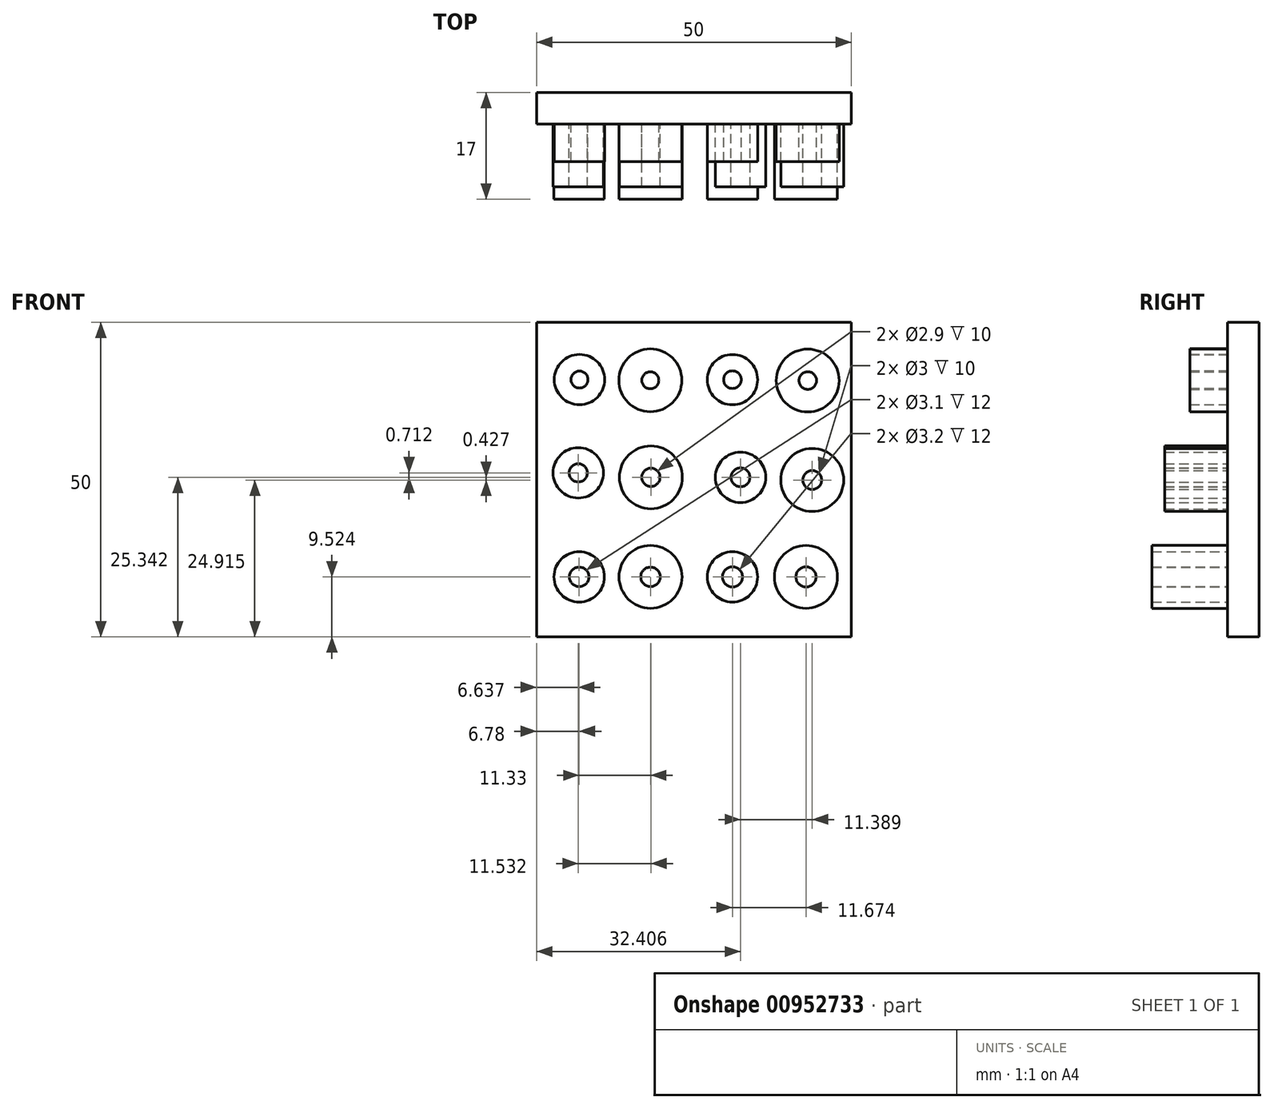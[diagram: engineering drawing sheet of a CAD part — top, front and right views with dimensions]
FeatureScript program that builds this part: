
annotation { "Feature Type Name" : "Feature", "Feature Type Description" : "" }
export const myFeature = defineFeature(function(context is Context, id is Id, definition is map)
    precondition{}
    {
        {
            var Q0;
            Q0=qCreatedBy(makeId("Front.planeOp"),FACE);
            var sketch = newSketch(context, id + "F0", { "sketchPlane" : qUnion([Q0])});
            skLineSegment(sketch, "E0.bottom", {"start": v(-25, 25) * mm, "end": v(25, 25) * mm});
            skLineSegment(sketch, "E0.top", {"start": v(-25, -25) * mm, "end": v(25, -25) * mm});
            skLineSegment(sketch, "E0.left", {"start": v(-25, 25) * mm, "end": v(-25, -25) * mm});
            skLineSegment(sketch, "E0.right", {"start": v(25, 25) * mm, "end": v(25, -25) * mm});
            skSolve(sketch);
        }
        {
            var Q0;
            Q0=qCreatedBy(makeId("Front.planeOp"),FACE);
            var sketch = newSketch(context, id + "F1", { "sketchPlane" : qUnion([Q0])});
            skPoint(sketch, "E1.middle", {"position": v(0.42, -1.18) * mm});
            skCircle(sketch, "E2", {"center": v(-18.17, 15.87) * mm, "radius": 1.35 * mm});
            skCircle(sketch, "E3", {"center": v(-18.17, 15.87) * mm, "radius": 4 * mm});
            skCircle(sketch, "E4", {"center": v(-6.92, 15.76) * mm, "radius": 5 * mm});
            skCircle(sketch, "E5", {"center": v(-6.92, 15.76) * mm, "radius": 1.35 * mm});
            skCircle(sketch, "E6", {"center": v(6.12, 15.86) * mm, "radius": 4 * mm});
            skCircle(sketch, "E7", {"center": v(6.12, 15.86) * mm, "radius": 1.4 * mm});
            skCircle(sketch, "E8", {"center": v(18.08, 15.72) * mm, "radius": 5 * mm});
            skCircle(sketch, "E9", {"center": v(18.08, 15.72) * mm, "radius": 1.4 * mm});
            skCircle(sketch, "E10", {"center": v(-18.36, 1.05) * mm, "radius": 4 * mm});
            skCircle(sketch, "E11", {"center": v(-18.36, 1.05) * mm, "radius": 1.45 * mm});
            skCircle(sketch, "E12", {"center": v(-6.83, 0.34) * mm, "radius": 5 * mm});
            skCircle(sketch, "E13", {"center": v(-6.83, 0.34) * mm, "radius": 1.45 * mm});
            skCircle(sketch, "E14", {"center": v(7.4, 0.34) * mm, "radius": 4 * mm});
            skCircle(sketch, "E15", {"center": v(7.4, 0.34) * mm, "radius": 1.5 * mm});
            skCircle(sketch, "E16", {"center": v(18.8, -0.09) * mm, "radius": 5 * mm});
            skCircle(sketch, "E17", {"center": v(18.8, -0.09) * mm, "radius": 1.5 * mm});
            skCircle(sketch, "E18", {"center": v(-18.22, -15.48) * mm, "radius": 4 * mm});
            skCircle(sketch, "E19", {"center": v(-18.22, -15.48) * mm, "radius": 1.55 * mm});
            skCircle(sketch, "E20", {"center": v(-6.89, -15.48) * mm, "radius": 5 * mm});
            skCircle(sketch, "E21", {"center": v(-6.89, -15.48) * mm, "radius": 1.55 * mm});
            skCircle(sketch, "E22", {"center": v(6.12, -15.48) * mm, "radius": 4 * mm});
            skCircle(sketch, "E23", {"center": v(6.12, -15.48) * mm, "radius": 1.6 * mm});
            skCircle(sketch, "E24", {"center": v(17.8, -15.48) * mm, "radius": 5 * mm});
            skCircle(sketch, "E25", {"center": v(17.8, -15.48) * mm, "radius": 1.6 * mm});
            skSolve(sketch);
        }
        {
            var Q0;
            Q0=makeQuery(id+"F0.imprint","IMPRINT",FACE,{"disambiguationData":[TD([[makeQuery(id+"F0.imprint","IMPRINT",EDGE,{"derivedFrom":sQuery(id+"F0.wireOp",EDGE,"E0.bottom")}),-1.0]])]});
            extrude(context, id + "F2", {"entities" : qUnion([Q0]), "depth" : -5 * mm, "offsetDistance" : 25 * mm});
        }
        {
            var Q0;
            Q0=makeQuery(id+"F1.imprint","IMPRINT",FACE,{"disambiguationData":[TD([[makeQuery(id+"F1.imprint","IMPRINT",EDGE,{"derivedFrom":sQuery(id+"F1.wireOp",EDGE,"E2")}),-1.0]])]});
            var Q1;
            Q1=makeQuery(id+"F1.imprint","IMPRINT",FACE,{"disambiguationData":[TD([[makeQuery(id+"F1.imprint","IMPRINT",EDGE,{"derivedFrom":sQuery(id+"F1.wireOp",EDGE,"E4")}),1.0]])]});
            var Q2;
            Q2=makeQuery(id+"F1.imprint","IMPRINT",FACE,{"disambiguationData":[TD([[makeQuery(id+"F1.imprint","IMPRINT",EDGE,{"derivedFrom":sQuery(id+"F1.wireOp",EDGE,"E6")}),1.0]])]});
            var Q3;
            Q3=makeQuery(id+"F1.imprint","IMPRINT",FACE,{"disambiguationData":[TD([[makeQuery(id+"F1.imprint","IMPRINT",EDGE,{"derivedFrom":sQuery(id+"F1.wireOp",EDGE,"E8")}),1.0]])]});
            extrude(context, id + "F3", {"entities" : qUnion([Q0, Q1, Q2, Q3]), "operationType" : NewBodyOperationType.ADD, "depth" : 6 * mm, "offsetDistance" : 25 * mm});
        }
        {
            var Q0;
            Q0=makeQuery(id+"F1.imprint","IMPRINT",FACE,{"disambiguationData":[TD([[makeQuery(id+"F1.imprint","IMPRINT",EDGE,{"derivedFrom":sQuery(id+"F1.wireOp",EDGE,"E10")}),1.0]])]});
            var Q1;
            Q1=makeQuery(id+"F1.imprint","IMPRINT",FACE,{"disambiguationData":[TD([[makeQuery(id+"F1.imprint","IMPRINT",EDGE,{"derivedFrom":sQuery(id+"F1.wireOp",EDGE,"E12")}),1.0]])]});
            var Q2;
            Q2=makeQuery(id+"F1.imprint","IMPRINT",FACE,{"disambiguationData":[TD([[makeQuery(id+"F1.imprint","IMPRINT",EDGE,{"derivedFrom":sQuery(id+"F1.wireOp",EDGE,"E14")}),1.0]])]});
            var Q3;
            Q3=makeQuery(id+"F1.imprint","IMPRINT",FACE,{"disambiguationData":[TD([[makeQuery(id+"F1.imprint","IMPRINT",EDGE,{"derivedFrom":sQuery(id+"F1.wireOp",EDGE,"E16")}),1.0]])]});
            extrude(context, id + "F4", {"entities" : qUnion([Q0, Q1, Q2, Q3]), "operationType" : NewBodyOperationType.ADD, "depth" : 10 * mm, "offsetDistance" : 25 * mm});
        }
        {
            var Q0;
            Q0=makeQuery(id+"F1.imprint","IMPRINT",FACE,{"disambiguationData":[TD([[makeQuery(id+"F1.imprint","IMPRINT",EDGE,{"derivedFrom":sQuery(id+"F1.wireOp",EDGE,"E20")}),1.0]])]});
            var Q1;
            Q1=makeQuery(id+"F1.imprint","IMPRINT",FACE,{"disambiguationData":[TD([[makeQuery(id+"F1.imprint","IMPRINT",EDGE,{"derivedFrom":sQuery(id+"F1.wireOp",EDGE,"E18")}),1.0]])]});
            var Q2;
            Q2=makeQuery(id+"F1.imprint","IMPRINT",FACE,{"disambiguationData":[TD([[makeQuery(id+"F1.imprint","IMPRINT",EDGE,{"derivedFrom":sQuery(id+"F1.wireOp",EDGE,"E22")}),1.0]])]});
            var Q3;
            Q3=makeQuery(id+"F1.imprint","IMPRINT",FACE,{"disambiguationData":[TD([[makeQuery(id+"F1.imprint","IMPRINT",EDGE,{"derivedFrom":sQuery(id+"F1.wireOp",EDGE,"E24")}),1.0]])]});
            extrude(context, id + "F5", {"entities" : qUnion([Q0, Q1, Q2, Q3]), "operationType" : NewBodyOperationType.ADD, "depth" : 12 * mm, "offsetDistance" : 25 * mm});
        }
    });
